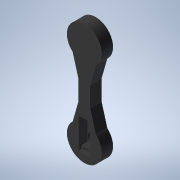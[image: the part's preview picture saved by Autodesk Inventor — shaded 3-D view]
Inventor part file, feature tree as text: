
AUTODESK INVENTOR PART (.ipt)
format: ipt  version: 2022 (Build 260153000, 153)  size: 237,056 bytes
history: native  units: in
note: dims shown in document units (in); Inventor stores cm internally (conversion verified against a paired STEP export)
features: extrude x13, sketch x13, thread x4, chamfer x1
ambient origin geometry x8: Origin, YZ Plane, XZ Plane, XY Plane, X Axis, Y Axis, Z Axis, Center Point
bodies: Solid1 (feature_tree)
feature tree (31):
  extrude  "Extrusion1"  Depth=5.9055in
  extrude  "Extrusion2"  Depth=2.3622in
  extrude  "Extrusion3"  Depth=0.7874in
  extrude  "Extrusion4"  Depth=1.4488in
  extrude  "Extrusion5"  Depth=0.2362in
  thread  "Thread1"  [1 undecoded]
  thread  "Thread2"  [1 undecoded]
  thread  "Thread3"  [1 undecoded]
  thread  "Thread4"  [1 undecoded]
  extrude  "Extrusion6"  Depth=0.2362in
  extrude  "Extrusion7"  Depth=0.2362in
  extrude  "Extrusion8"  Depth=0.1969in
  extrude  "Extrusion9"  Depth=0.1063in
  extrude  "Extrusion10"  Depth=0.1063in
  extrude  "Extrusion11"  Depth=0.3937in TaperAngle=0.0deg
  extrude  "Extrusion12"  Depth=0.3937in TaperAngle=0.0deg
  extrude  "Extrusion13"  Depth=0.3937in TaperAngle=0.0deg
  chamfer  "Chamfer2"  Distance=0.7874in
  sketch  "Sketch1"  dims[d0=1.5748in d1=5.9055in]
  sketch  "Sketch2"  dims[d2=2.3622in d3=2.3622in]
  sketch  "Sketch3"  dims[d4=0.7874in d5=0.0in d6=0.7874in]
  sketch  "Sketch4"  dims[d7=0.6693in d8=1.4488in]
  sketch  "Sketch5"  dims[d9=0.2362in d10=0.2362in d11=0.1181in d12=0.6299in d13=0.0in d14=0.7874in d15=2.7451in d16=0.0in]
  sketch  "Sketch6"  dims[d17=0.2362in d18=0.2362in]
  sketch  "Sketch7"  dims[d19=0.2362in d20=0.0in d21=0.1181in]
  sketch  "Sketch8"  dims[d22=0.1969in d23=0.1969in]
  sketch  "Sketch9"  dims[d24=0.1063in d25=0.1063in]
  sketch  "Sketch10"  dims[d26=0.1181in d27=0.1063in]
  sketch  "Sketch11"  dims[d28=0.1063in d29=0.3937in d30=0.0in]
  sketch  "Sketch12"  dims[d31=0.3937in d32=0.0in d33=0.3937in d34=0.0in]
  sketch  "Sketch13"  dims[d35=0.3937in d36=0.0in d37=0.3937in d38=0.0in d39=0.7874in d40=5.9055in d41=0.7874in d42=0.0787in d43=0.0787in d44=0.0787in d45=1.5438in d46=0.0in d47=0.7874in d48=0.6299in d49=0.0in d53=0.7874in d54=2.7559in d55=2.7559in d56=2.2313in d57=0.0in d58=0.6299in d59=0.0in d60=0.7874in d61=0.6299in d62=0.0in d63=0.7874in d64=0.0in d65=1.9626in d66=0.0in d67=0.0787in d68=0.0787in d69=1.6624in d70=0.0in d71=0.4724in d72=0.0787in d73=45.0deg]
note: 4 required parameter values undecoded (feature->parameter linkage not recoverable at this tier; creation-order binding heuristic only, values carry confidence <= 0.55)
